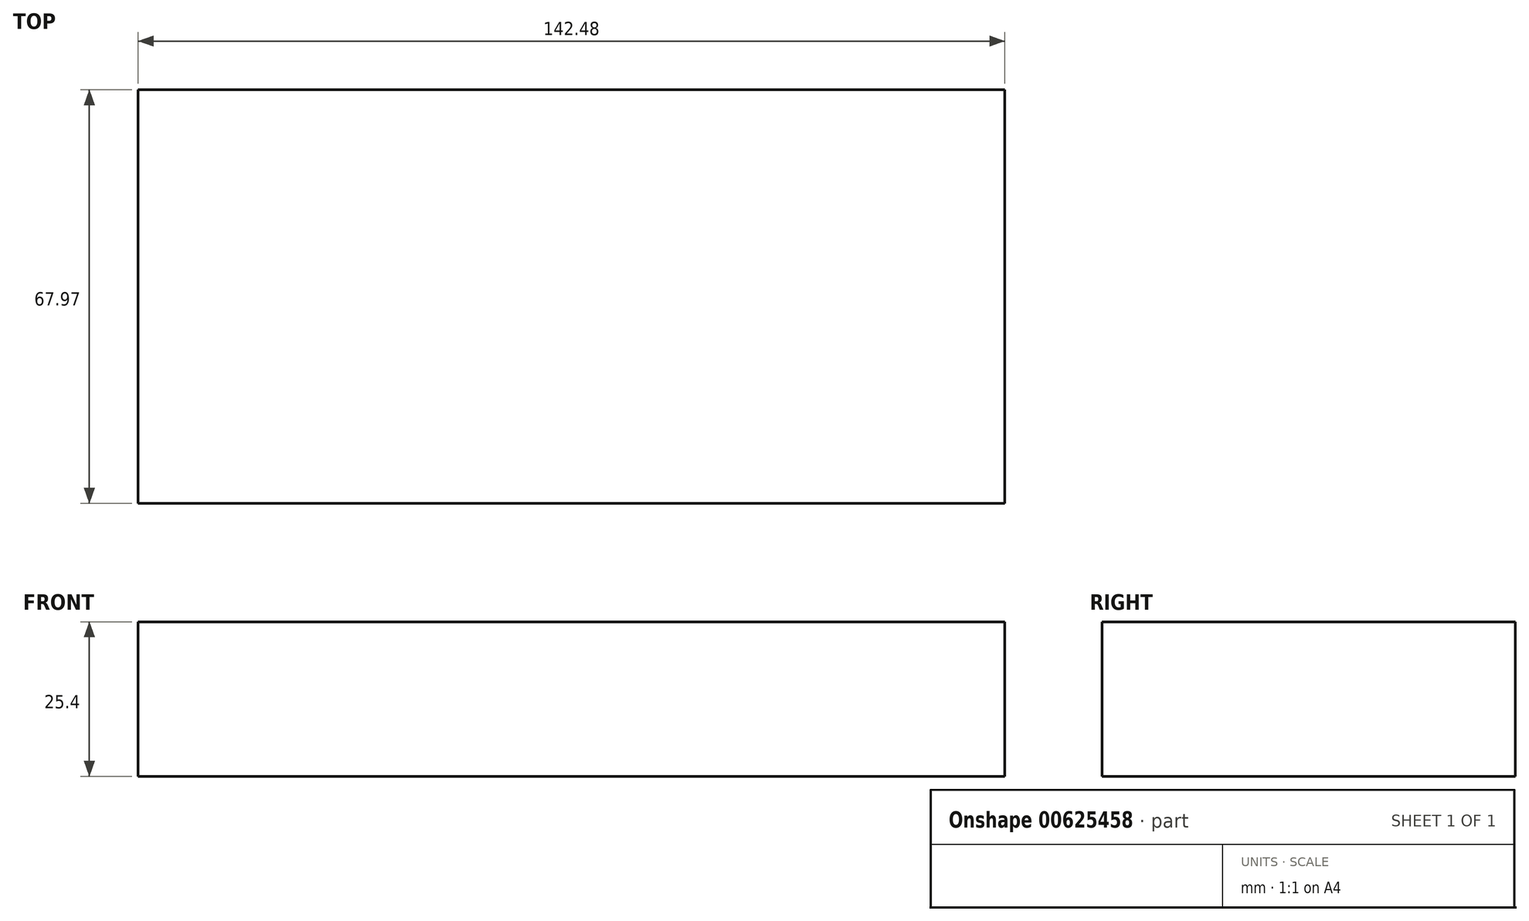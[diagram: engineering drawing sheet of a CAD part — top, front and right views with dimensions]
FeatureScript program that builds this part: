
annotation { "Feature Type Name" : "Feature", "Feature Type Description" : "" }
export const myFeature = defineFeature(function(context is Context, id is Id, definition is map)
    precondition{}
    {
        {
            var Q0;
            Q0=qCreatedBy(makeId("Top.planeOp"),FACE);
            var sketch = newSketch(context, id + "F0", { "sketchPlane" : qUnion([Q0])});
            skLineSegment(sketch, "E0.bottom", {"start": v(-66.4, 30.49) * mm, "end": v(76.07, 30.49) * mm});
            skLineSegment(sketch, "E0.top", {"start": v(-66.4, -37.48) * mm, "end": v(76.07, -37.48) * mm});
            skLineSegment(sketch, "E0.left", {"start": v(-66.4, 30.49) * mm, "end": v(-66.4, -37.48) * mm});
            skLineSegment(sketch, "E0.right", {"start": v(76.07, 30.49) * mm, "end": v(76.07, -37.48) * mm});
            skSolve(sketch);
        }
        {
            var Q0;
            Q0 = qConstructionFilter(qBodyType(qCreatedBy(id + "F0" ,EDGE), BodyType.WIRE), ConstructionObject.NO);
            extrude(context, id + "F1", {"bodyType" : ToolBodyType.SURFACE, "surfaceEntities" : qUnion([Q0]), "depth" : 25.4 * mm, "offsetDistance" : 25.4 * mm});
        }
        {
            var Q0;
            Q0=makeQuery(id+"F1.opExtrude","SWEPT_FACE",FACE,{"disambiguationData":[OSD([sQuery(id+"F0.wireOp",EDGE,"E0.bottom")])]});
            var Q1;
            Q1=makeQuery(id+"F1.opExtrude","SWEPT_FACE",FACE,{"disambiguationData":[OSD([sQuery(id+"F0.wireOp",EDGE,"E0.top")])]});
            extrude(context, id + "F2", {"entities" : qUnion([Q0]), "endBound" : BoundingType.UP_TO_SURFACE, "oppositeDirection" : true, "depth" : 25.4 * mm, "endBoundEntityFace" : qUnion([Q1]), "offsetDistance" : 25.4 * mm});
        }
    });
